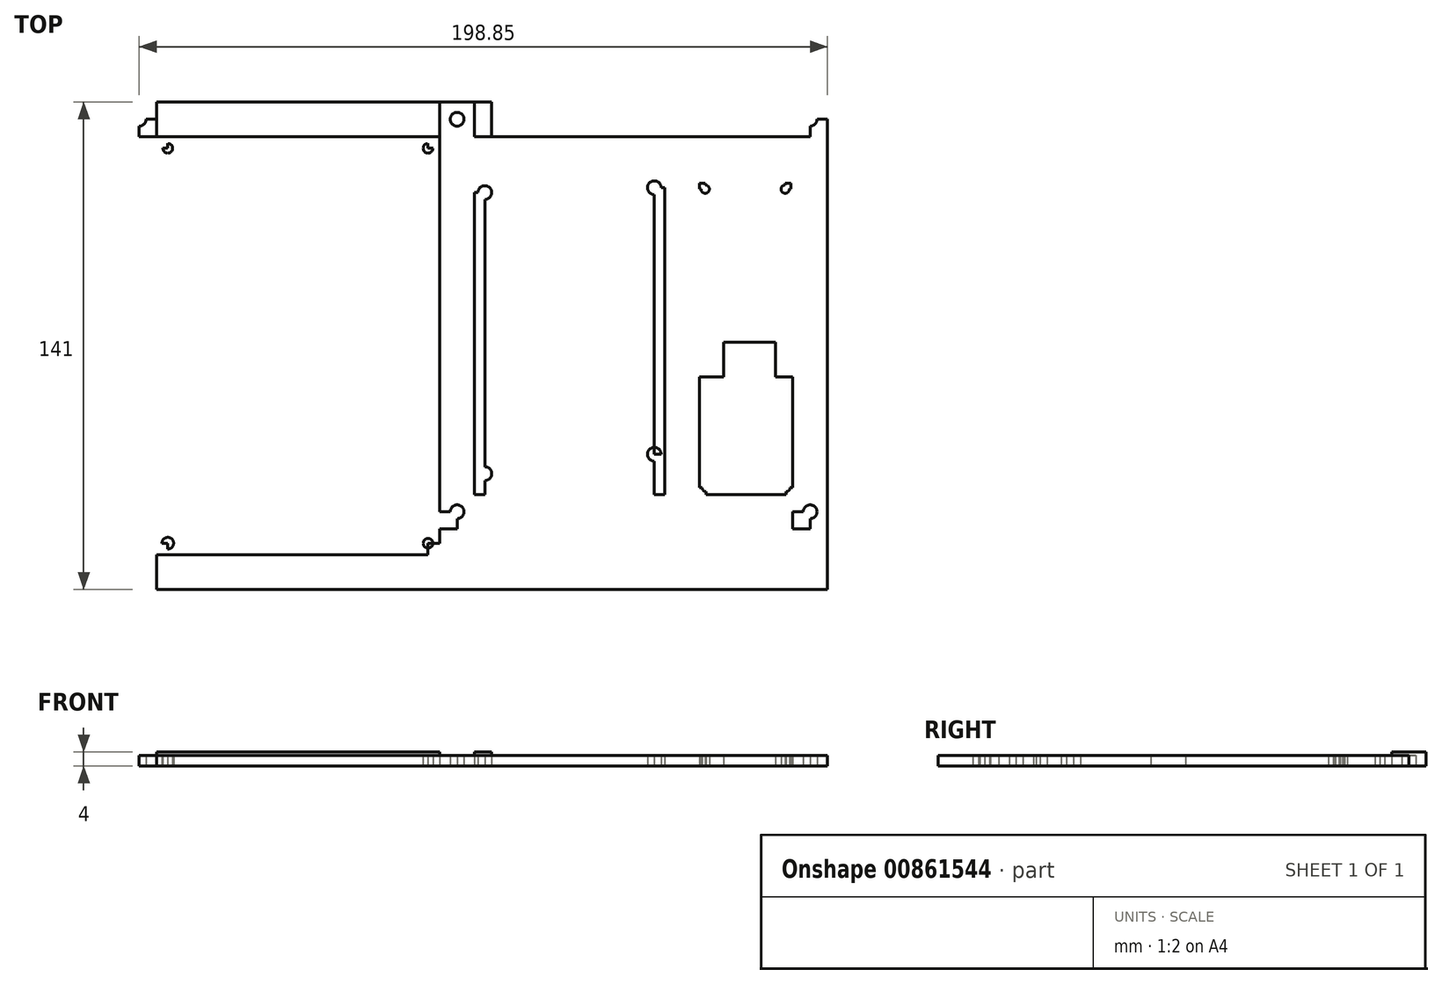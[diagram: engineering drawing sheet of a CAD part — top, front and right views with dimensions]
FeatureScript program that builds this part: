
annotation { "Feature Type Name" : "Feature", "Feature Type Description" : "" }
export const myFeature = defineFeature(function(context is Context, id is Id, definition is map)
    precondition{}
    {
        {
            var Q0;
            Q0=qCreatedBy(makeId("Top.planeOp"),FACE);
            var sketch = newSketch(context, id + "F0", { "sketchPlane" : qUnion([Q0])});
            skLineSegment(sketch, "E0.bottom", {"start": v(-139.34, -1.26) * mm, "end": v(-129.34, -1.26) * mm});
            skLineSegment(sketch, "E0.top", {"start": v(-139.34, -11.26) * mm, "end": v(-129.34, -11.26) * mm});
            skLineSegment(sketch, "E0.left", {"start": v(-139.34, -1.26) * mm, "end": v(-139.34, -11.26) * mm});
            skLineSegment(sketch, "E0.right", {"start": v(-129.34, -1.26) * mm, "end": v(-129.34, -11.26) * mm});
            skLineSegment(sketch, "E1.bottom", {"start": v(-129.34, -11.26) * mm, "end": v(-74.34, -11.26) * mm});
            skLineSegment(sketch, "E1.top", {"start": v(-129.34, -114.76) * mm, "end": v(-74.34, -114.76) * mm});
            skLineSegment(sketch, "E1.left", {"start": v(-129.34, -11.26) * mm, "end": v(-129.34, -114.76) * mm});
            skLineSegment(sketch, "E1.right", {"start": v(-74.34, -11.26) * mm, "end": v(-74.34, -114.76) * mm});
            skLineSegment(sketch, "E2", {"start": v(-74.34, -114.76) * mm, "end": v(-64.34, -114.76) * mm});
            skLineSegment(sketch, "E3.bottom", {"start": v(-64.34, -114.76) * mm, "end": v(-37.34, -114.76) * mm});
            skLineSegment(sketch, "E3.top", {"start": v(-64.34, -80.76) * mm, "end": v(-37.34, -80.76) * mm});
            skLineSegment(sketch, "E3.left", {"start": v(-64.34, -114.76) * mm, "end": v(-64.34, -80.76) * mm});
            skLineSegment(sketch, "E3.right", {"start": v(-37.34, -114.76) * mm, "end": v(-37.34, -80.76) * mm});
            skLineSegment(sketch, "E4", {"start": v(-37.34, -80.76) * mm, "end": v(-42.34, -80.76) * mm});
            skLineSegment(sketch, "E5.bottom", {"start": v(-42.34, -80.76) * mm, "end": v(-57.34, -80.76) * mm});
            skLineSegment(sketch, "E5.top", {"start": v(-42.34, -70.76) * mm, "end": v(-57.34, -70.76) * mm});
            skLineSegment(sketch, "E5.left", {"start": v(-42.34, -80.76) * mm, "end": v(-42.34, -70.76) * mm});
            skLineSegment(sketch, "E5.right", {"start": v(-57.34, -80.76) * mm, "end": v(-57.34, -70.76) * mm});
            skLineSegment(sketch, "E6", {"start": v(-64.34, -80.76) * mm, "end": v(-64.34, -60.76) * mm});
            skLineSegment(sketch, "E7.bottom", {"start": v(-64.34, -60.76) * mm, "end": v(-37.84, -60.76) * mm});
            skLineSegment(sketch, "E7.top", {"start": v(-64.34, -24.76) * mm, "end": v(-37.84, -24.76) * mm});
            skLineSegment(sketch, "E7.left", {"start": v(-64.34, -60.76) * mm, "end": v(-64.34, -24.76) * mm});
            skLineSegment(sketch, "E7.right", {"start": v(-37.84, -60.76) * mm, "end": v(-37.84, -24.76) * mm});
            skLineSegment(sketch, "E8", {"start": v(-74.34, -11.26) * mm, "end": v(-27.34, -11.26) * mm});
            skLineSegment(sketch, "E9.bottom", {"start": v(-129.34, -114.76) * mm, "end": v(-139.34, -114.76) * mm});
            skLineSegment(sketch, "E9.top", {"start": v(-129.34, -124.76) * mm, "end": v(-139.34, -124.76) * mm});
            skLineSegment(sketch, "E9.left", {"start": v(-129.34, -114.76) * mm, "end": v(-129.34, -124.76) * mm});
            skLineSegment(sketch, "E9.right", {"start": v(-139.34, -114.76) * mm, "end": v(-139.34, -124.76) * mm});
            skLineSegment(sketch, "E10.bottom", {"start": v(-37.34, -114.76) * mm, "end": v(-27.34, -114.76) * mm});
            skLineSegment(sketch, "E10.top", {"start": v(-37.34, -124.76) * mm, "end": v(-27.34, -124.76) * mm});
            skLineSegment(sketch, "E10.left", {"start": v(-37.34, -114.76) * mm, "end": v(-37.34, -124.76) * mm});
            skLineSegment(sketch, "E10.right", {"start": v(-27.34, -114.76) * mm, "end": v(-27.34, -124.76) * mm});
            skLineSegment(sketch, "E11.top", {"start": v(-139.34, -124.76) * mm, "end": v(-37.34, -124.76) * mm});
            skLineSegment(sketch, "E12", {"start": v(-129.34, -11.26) * mm, "end": v(-124.34, -11.26) * mm});
            skLineSegment(sketch, "E13", {"start": v(-124.34, -11.26) * mm, "end": v(-124.34, -1.26) * mm});
            skLineSegment(sketch, "E14", {"start": v(-74.34, -11.26) * mm, "end": v(-79.34, -11.26) * mm});
            skLineSegment(sketch, "E15", {"start": v(-79.34, -11.26) * mm, "end": v(-79.34, -1.26) * mm});
            skLineSegment(sketch, "E16.bottom", {"start": v(-129.34, -11.26) * mm, "end": v(-126.54, -11.26) * mm});
            skLineSegment(sketch, "E16.left", {"start": v(-129.34, -11.26) * mm, "end": v(-129.34, -14.06) * mm});
            skLineSegment(sketch, "E17.bottom", {"start": v(-129.34, -114.76) * mm, "end": v(-126.34, -114.76) * mm});
            skLineSegment(sketch, "E17.left", {"start": v(-129.34, -114.76) * mm, "end": v(-129.34, -111.76) * mm});
            skLineSegment(sketch, "E18.bottom", {"start": v(-74.34, -114.76) * mm, "end": v(-77.2, -114.76) * mm});
            skLineSegment(sketch, "E18.left", {"start": v(-74.34, -114.76) * mm, "end": v(-74.34, -111.9) * mm});
            skLineSegment(sketch, "E19.bottom", {"start": v(-74.34, -11.26) * mm, "end": v(-77.34, -11.26) * mm});
            skLineSegment(sketch, "E19.left", {"start": v(-74.34, -11.26) * mm, "end": v(-74.34, -14.26) * mm});
            skLineSegment(sketch, "E20.left", {"start": v(-27.34, -11.26) * mm, "end": v(-27.34, -14.66) * mm});
            skLineSegment(sketch, "E21.bottom", {"start": v(-37.84, -60.76) * mm, "end": v(-39.6, -60.76) * mm});
            skLineSegment(sketch, "E21.left", {"start": v(-37.84, -60.76) * mm, "end": v(-37.84, -59) * mm});
            skLineSegment(sketch, "E22.bottom", {"start": v(-37.84, -24.76) * mm, "end": v(-39.54, -24.76) * mm});
            skLineSegment(sketch, "E22.top", {"start": v(-37.84, -26.46) * mm, "end": v(-39.54, -26.46) * mm});
            skLineSegment(sketch, "E22.left", {"start": v(-37.84, -24.76) * mm, "end": v(-37.84, -26.46) * mm});
            skLineSegment(sketch, "E22.right", {"start": v(-39.54, -24.76) * mm, "end": v(-39.54, -26.46) * mm});
            skLineSegment(sketch, "E23.bottom", {"start": v(-64.34, -24.76) * mm, "end": v(-62.64, -24.76) * mm});
            skLineSegment(sketch, "E23.top", {"start": v(-64.34, -26.46) * mm, "end": v(-62.64, -26.46) * mm});
            skLineSegment(sketch, "E23.left", {"start": v(-64.34, -24.76) * mm, "end": v(-64.34, -26.46) * mm});
            skLineSegment(sketch, "E23.right", {"start": v(-62.64, -24.76) * mm, "end": v(-62.64, -26.46) * mm});
            skLineSegment(sketch, "E24.bottom", {"start": v(-64.34, -60.76) * mm, "end": v(-62.6, -60.76) * mm});
            skLineSegment(sketch, "E24.left", {"start": v(-64.34, -60.76) * mm, "end": v(-64.34, -59) * mm});
            skLineSegment(sketch, "E25.bottom", {"start": v(-64.34, -114.76) * mm, "end": v(-62.4, -114.76) * mm});
            skLineSegment(sketch, "E25.top", {"start": v(-64.34, -112.8) * mm, "end": v(-62.4, -112.8) * mm});
            skLineSegment(sketch, "E25.left", {"start": v(-64.34, -114.76) * mm, "end": v(-64.34, -112.8) * mm});
            skLineSegment(sketch, "E25.right", {"start": v(-62.4, -114.76) * mm, "end": v(-62.4, -112.8) * mm});
            skLineSegment(sketch, "E26.bottom", {"start": v(-37.34, -114.76) * mm, "end": v(-39.3, -114.76) * mm});
            skLineSegment(sketch, "E26.top", {"start": v(-37.34, -112.8) * mm, "end": v(-39.3, -112.8) * mm});
            skLineSegment(sketch, "E26.left", {"start": v(-37.34, -114.76) * mm, "end": v(-37.34, -112.8) * mm});
            skLineSegment(sketch, "E26.right", {"start": v(-39.3, -114.76) * mm, "end": v(-39.3, -112.8) * mm});
            skLineSegment(sketch, "E27.bottom", {"start": v(-37.34, -80.76) * mm, "end": v(-39.3, -80.76) * mm});
            skLineSegment(sketch, "E27.top", {"start": v(-37.34, -82.7) * mm, "end": v(-39.3, -82.7) * mm});
            skLineSegment(sketch, "E27.left", {"start": v(-37.34, -80.76) * mm, "end": v(-37.34, -82.7) * mm});
            skLineSegment(sketch, "E27.right", {"start": v(-39.3, -80.76) * mm, "end": v(-39.3, -82.7) * mm});
            skLineSegment(sketch, "E28.bottom", {"start": v(-64.34, -80.76) * mm, "end": v(-62.4, -80.76) * mm});
            skLineSegment(sketch, "E28.top", {"start": v(-64.34, -82.7) * mm, "end": v(-62.4, -82.7) * mm});
            skLineSegment(sketch, "E28.left", {"start": v(-64.34, -80.76) * mm, "end": v(-64.34, -82.7) * mm});
            skLineSegment(sketch, "E28.right", {"start": v(-62.4, -80.76) * mm, "end": v(-62.4, -82.7) * mm});
            skCircle(sketch, "E29", {"center": v(-39.3, -112.8) * mm, "radius": 1.15 * mm});
            skCircle(sketch, "E30", {"center": v(-62.4, -112.8) * mm, "radius": 1.15 * mm});
            skCircle(sketch, "E31", {"center": v(-62.4, -82.7) * mm, "radius": 1.15 * mm});
            skCircle(sketch, "E32", {"center": v(-39.3, -82.7) * mm, "radius": 1.15 * mm});
            skCircle(sketch, "E33", {"center": v(-62.64, -26.46) * mm, "radius": 1.2 * mm});
            skCircle(sketch, "E34", {"center": v(-39.54, -26.46) * mm, "radius": 1.2 * mm});
            skLineSegment(sketch, "E35.top", {"start": v(-37.34, -124.76) * mm, "end": v(-139.34, -124.76) * mm});
            skLineSegment(sketch, "E36.bottom", {"start": v(-139.34, -124.76) * mm, "end": v(-134.34, -124.76) * mm});
            skLineSegment(sketch, "E36.top", {"start": v(-139.34, -119.76) * mm, "end": v(-134.34, -119.76) * mm});
            skLineSegment(sketch, "E36.left", {"start": v(-139.34, -124.76) * mm, "end": v(-139.34, -119.76) * mm});
            skLineSegment(sketch, "E36.right", {"start": v(-134.34, -124.76) * mm, "end": v(-134.34, -119.76) * mm});
            skCircle(sketch, "E37", {"center": v(-134.34, -119.76) * mm, "radius": 2 * mm});
            skLineSegment(sketch, "E38.bottom", {"start": v(-37.34, -124.76) * mm, "end": v(-32.34, -124.76) * mm});
            skLineSegment(sketch, "E38.top", {"start": v(-37.34, -119.76) * mm, "end": v(-32.34, -119.76) * mm});
            skLineSegment(sketch, "E38.left", {"start": v(-37.34, -124.76) * mm, "end": v(-37.34, -119.76) * mm});
            skLineSegment(sketch, "E38.right", {"start": v(-32.34, -124.76) * mm, "end": v(-32.34, -119.76) * mm});
            skCircle(sketch, "E39", {"center": v(-32.34, -119.76) * mm, "radius": 2 * mm});
            skLineSegment(sketch, "E40.bottom", {"start": v(-139.34, -1.26) * mm, "end": v(-134.34, -1.26) * mm});
            skLineSegment(sketch, "E40.top", {"start": v(-139.34, -6.26) * mm, "end": v(-134.34, -6.26) * mm});
            skLineSegment(sketch, "E40.left", {"start": v(-139.34, -1.26) * mm, "end": v(-139.34, -6.26) * mm});
            skLineSegment(sketch, "E40.right", {"start": v(-134.34, -1.26) * mm, "end": v(-134.34, -6.26) * mm});
            skCircle(sketch, "E41", {"center": v(-134.34, -6.26) * mm, "radius": 2 * mm});
            skLineSegment(sketch, "E42.bottom", {"start": v(-129.34, -11.26) * mm, "end": v(-126.34, -11.26) * mm});
            skLineSegment(sketch, "E42.left", {"start": v(-129.34, -11.26) * mm, "end": v(-129.34, -27.96) * mm});
            skLineSegment(sketch, "E43.top", {"start": v(-129.34, -108.76) * mm, "end": v(-126.34, -108.76) * mm});
            skLineSegment(sketch, "E43.left", {"start": v(-129.34, -114.76) * mm, "end": v(-129.34, -108.76) * mm});
            skLineSegment(sketch, "E43.right", {"start": v(-126.34, -114.76) * mm, "end": v(-126.34, -108.76) * mm});
            skLineSegment(sketch, "E44.bottom", {"start": v(-74.34, -114.76) * mm, "end": v(-77.34, -114.76) * mm});
            skLineSegment(sketch, "E44.top", {"start": v(-74.34, -103.16) * mm, "end": v(-77.34, -103.16) * mm});
            skLineSegment(sketch, "E44.left", {"start": v(-74.34, -114.76) * mm, "end": v(-74.34, -103.16) * mm});
            skLineSegment(sketch, "E44.right", {"start": v(-77.34, -114.76) * mm, "end": v(-77.34, -103.16) * mm});
            skLineSegment(sketch, "E45.top", {"start": v(-74.34, -26.06) * mm, "end": v(-77.34, -26.06) * mm});
            skLineSegment(sketch, "E45.left", {"start": v(-74.34, -114.76) * mm, "end": v(-74.34, -26.06) * mm});
            skLineSegment(sketch, "E45.right", {"start": v(-77.34, -114.76) * mm, "end": v(-77.34, -26.06) * mm});
            skLineSegment(sketch, "E46.top", {"start": v(-129.34, -27.46) * mm, "end": v(-126.34, -27.46) * mm});
            skLineSegment(sketch, "E46.left", {"start": v(-129.34, -114.76) * mm, "end": v(-129.34, -27.46) * mm});
            skLineSegment(sketch, "E46.right", {"start": v(-126.34, -114.76) * mm, "end": v(-126.34, -27.46) * mm});
            skCircle(sketch, "E47", {"center": v(-126.34, -108.76) * mm, "radius": 2 * mm});
            skCircle(sketch, "E48", {"center": v(-126.34, -27.46) * mm, "radius": 2 * mm});
            skCircle(sketch, "E49", {"center": v(-77.34, -26.06) * mm, "radius": 2 * mm});
            skCircle(sketch, "E50", {"center": v(-77.34, -103.16) * mm, "radius": 2 * mm});
            skLineSegment(sketch, "E51", {"start": v(-139.34, -1.26) * mm, "end": v(-83.34, -1.26) * mm});
            skLineSegment(sketch, "E52.bottom", {"start": v(-83.34, -1.26) * mm, "end": v(-139.34, -1.26) * mm});
            skLineSegment(sketch, "E53.MirrorCS", {"start": v(-139.34, -132.26) * mm, "end": v(-139.34, -11.26) * mm});
            skLineSegment(sketch, "E54.MirrorCS", {"start": v(-221.2, -11.26) * mm, "end": v(-139.2, -11.26) * mm});
            skLineSegment(sketch, "E55.MirrorCS", {"start": v(-221.2, -132.26) * mm, "end": v(-139.2, -132.26) * mm});
            skCircle(sketch, "E56.MirrorC", {"center": v(-142.74, -128.86) * mm, "radius": 1.4 * mm});
            skCircle(sketch, "E57.MirrorC", {"center": v(-217.94, -128.86) * mm, "radius": 1.7 * mm});
            skCircle(sketch, "E58.MirrorC", {"center": v(-217.94, -14.66) * mm, "radius": 1.4 * mm});
            skCircle(sketch, "E59.MirrorC", {"center": v(-142.74, -14.66) * mm, "radius": 1.4 * mm});
            skLineSegment(sketch, "E60.MirrorCS", {"start": v(-142.74, -11.26) * mm, "end": v(-142.74, -14.66) * mm});
            skLineSegment(sketch, "E61.MirrorCS", {"start": v(-139.34, -14.66) * mm, "end": v(-142.74, -14.66) * mm});
            skLineSegment(sketch, "E62.MirrorCS", {"start": v(-217.94, -11.26) * mm, "end": v(-217.94, -14.66) * mm});
            skLineSegment(sketch, "E63.MirrorCS", {"start": v(-221.34, -14.66) * mm, "end": v(-217.94, -14.66) * mm});
            skLineSegment(sketch, "E64.MirrorCS", {"start": v(-142.74, -132.26) * mm, "end": v(-142.74, -128.86) * mm});
            skLineSegment(sketch, "E65.MirrorCS", {"start": v(-139.34, -128.86) * mm, "end": v(-142.74, -128.86) * mm});
            skLineSegment(sketch, "E66.MirrorCS", {"start": v(-221.34, -128.86) * mm, "end": v(-217.94, -128.86) * mm});
            skLineSegment(sketch, "E67.MirrorCS", {"start": v(-217.94, -132.26) * mm, "end": v(-217.94, -128.86) * mm});
            skLineSegment(sketch, "E68.MirrorCS", {"start": v(-27.34, -1.26) * mm, "end": v(-231.2, -1.26) * mm});
            skLineSegment(sketch, "E69", {"start": v(-221.2, -11.26) * mm, "end": v(-221.2, -1.26) * mm});
            skLineSegment(sketch, "E70", {"start": v(-221.2, -132.26) * mm, "end": v(-221.2, -11.26) * mm});
            skLineSegment(sketch, "E71", {"start": v(-221.2, -132.26) * mm, "end": v(-231.34, -132.26) * mm});
            skLineSegment(sketch, "E72", {"start": v(-27.34, -11.26) * mm, "end": v(-27.34, -1.26) * mm});
            skLineSegment(sketch, "E73.bottom", {"start": v(-221.2, -132.26) * mm, "end": v(-231.2, -132.26) * mm});
            skLineSegment(sketch, "E73.top", {"start": v(-221.2, -142.26) * mm, "end": v(-231.2, -142.26) * mm});
            skLineSegment(sketch, "E73.left", {"start": v(-221.2, -132.26) * mm, "end": v(-221.2, -142.26) * mm});
            skLineSegment(sketch, "E73.right", {"start": v(-231.2, -132.26) * mm, "end": v(-231.2, -142.26) * mm});
            skLineSegment(sketch, "E74.bottom", {"start": v(-221.2, -142.26) * mm, "end": v(-139.2, -142.26) * mm});
            skLineSegment(sketch, "E74.left", {"start": v(-221.2, -142.26) * mm, "end": v(-221.2, -132.26) * mm});
            skLineSegment(sketch, "E75", {"start": v(-27.34, -114.76) * mm, "end": v(-27.34, -11.26) * mm});
            skLineSegment(sketch, "E76", {"start": v(-231.2, -132.26) * mm, "end": v(-231.2, -1.26) * mm});
            skLineSegment(sketch, "E77.bottom", {"start": v(-129.34, -124.76) * mm, "end": v(-139.2, -124.76) * mm});
            skLineSegment(sketch, "E77.top", {"start": v(-129.34, -142.26) * mm, "end": v(-139.2, -142.26) * mm});
            skLineSegment(sketch, "E77.left", {"start": v(-129.34, -124.76) * mm, "end": v(-129.34, -142.26) * mm});
            skLineSegment(sketch, "E78", {"start": v(-139.2, -142.26) * mm, "end": v(-139.34, -132.26) * mm});
            skLineSegment(sketch, "E79.bottom", {"start": v(-231.2, -142.26) * mm, "end": v(-226.2, -142.26) * mm});
            skLineSegment(sketch, "E79.top", {"start": v(-231.2, -137.4) * mm, "end": v(-226.2, -137.4) * mm});
            skLineSegment(sketch, "E79.left", {"start": v(-231.2, -142.26) * mm, "end": v(-231.2, -137.4) * mm});
            skLineSegment(sketch, "E79.right", {"start": v(-226.2, -142.26) * mm, "end": v(-226.2, -137.4) * mm});
            skCircle(sketch, "E80", {"center": v(-226.2, -137.4) * mm, "radius": 2 * mm});
            skLineSegment(sketch, "E81.bottom", {"start": v(-221.2, -11.26) * mm, "end": v(-226.2, -11.26) * mm});
            skLineSegment(sketch, "E81.top", {"start": v(-221.2, -6.26) * mm, "end": v(-226.2, -6.26) * mm});
            skLineSegment(sketch, "E81.left", {"start": v(-221.2, -11.26) * mm, "end": v(-221.2, -6.26) * mm});
            skLineSegment(sketch, "E81.right", {"start": v(-226.2, -11.26) * mm, "end": v(-226.2, -6.26) * mm});
            skCircle(sketch, "E82", {"center": v(-226.2, -6.26) * mm, "radius": 2 * mm});
            skLineSegment(sketch, "E83.bottom", {"start": v(-27.34, -11.26) * mm, "end": v(-32.34, -11.26) * mm});
            skLineSegment(sketch, "E83.top", {"start": v(-27.34, -6.26) * mm, "end": v(-32.34, -6.26) * mm});
            skLineSegment(sketch, "E83.left", {"start": v(-27.34, -11.26) * mm, "end": v(-27.34, -6.26) * mm});
            skLineSegment(sketch, "E83.right", {"start": v(-32.34, -11.26) * mm, "end": v(-32.34, -6.26) * mm});
            skCircle(sketch, "E84", {"center": v(-32.34, -6.26) * mm, "radius": 2 * mm});
            skLineSegment(sketch, "E85.bottom", {"start": v(-129.34, -142.26) * mm, "end": v(-27.34, -142.26) * mm});
            skLineSegment(sketch, "E85.top", {"start": v(-129.34, -124.76) * mm, "end": v(-27.34, -124.76) * mm});
            skLineSegment(sketch, "E85.left", {"start": v(-129.34, -142.26) * mm, "end": v(-129.34, -124.76) * mm});
            skLineSegment(sketch, "E85.right", {"start": v(-27.34, -142.26) * mm, "end": v(-27.34, -124.76) * mm});
            skSolve(sketch);
        }
        {
            var Q0;
            Q0=makeQuery(id+"F0.imprint","IMPRINT",FACE,{"disambiguationData":[TD([[makeQuery(id+"F0.imprint","IMPRINT",EDGE,{"derivedFrom":sQuery(id+"F0.wireOp",EDGE,"E1.right")}),1.0]])]});
            var Q1;
            Q1=makeQuery(id+"F0.imprint","IMPRINT",FACE,{"disambiguationData":[TD([[makeQuery(id+"F0.imprint","IMPRINT",EDGE,{"derivedFrom":sQuery(id+"F0.wireOp",EDGE,"E10.bottom")}),-1.0]])]});
            var Q2;
            Q2=makeQuery(id+"F0.imprint","IMPRINT",FACE,{"disambiguationData":[TD([[makeQuery(id+"F0.imprint","IMPRINT",EDGE,{"derivedFrom":sQuery(id+"F0.wireOp",EDGE,"E1.top")}),-1.0]])]});
            var Q3;
            Q3=makeQuery(id+"F0.imprint","IMPRINT",FACE,{"disambiguationData":[TD([[makeQuery(id+"F0.imprint","IMPRINT",EDGE,{"derivedFrom":sQuery(id+"F0.wireOp",EDGE,"E9.bottom")}),1.0]])]});
            var Q4;
            Q4=makeQuery(id+"F0.imprint","IMPRINT",FACE,{"disambiguationData":[TD([[makeQuery(id+"F0.imprint","IMPRINT",EDGE,{"derivedFrom":sQuery(id+"F0.wireOp",EDGE,"97myMdQA-agTY-EE5a-eSU0-3Ky6piHqa90I.left")}),1.0]])]});
            var Q5;
            Q5=makeQuery(id+"F0.imprint","IMPRINT",FACE,{"disambiguationData":[TD([[makeQuery(id+"F0.imprint","IMPRINT",EDGE,{"derivedFrom":sQuery(id+"F0.wireOp",EDGE,"E0.bottom")}),-1.0]])]});
            var Q6;
            {var subQ0=sQuery(id+"F0.wireOp",EDGE,"E0.right");Q6=makeQuery(id+"F0.imprint","IMPRINT",FACE,{"disambiguationData":[TD([[makeQuery(id+"F0.imprint","IMPRINT",EDGE,{"derivedFrom":subQ0}),1.0]])]});}
            var Q7;
            {var subQ2=sQuery(id+"F0.wireOp",EDGE,"97myMdQA-agTY-EE5a-eSU0-3Ky6piHqa90I.right");Q7=makeQuery(id+"F0.imprint","IMPRINT",FACE,{"disambiguationData":[TD([[makeQuery(id+"F0.imprint","IMPRINT",EDGE,{"derivedFrom":subQ2}),-1.0]])]});}
            var Q8;
            {var subQ0=sQuery(id+"F0.wireOp",EDGE,"E10.top");Q8=makeQuery(id+"F0.imprint","IMPRINT",FACE,{"disambiguationData":[TD([[makeQuery(id+"F0.imprint","IMPRINT",EDGE,{"derivedFrom":subQ0}),-1.0]])]});}
            var Q9;
            {var subQ1=sQuery(id+"F0.wireOp",EDGE,"R2WY0SRa-AH7d-UwmP-SjNj-uamWJIKeu4LY.bottom");Q9=makeQuery(id+"F0.imprint","IMPRINT",FACE,{"disambiguationData":[TD([[makeQuery(id+"F0.imprint","IMPRINT",EDGE,{"derivedFrom":subQ1}),1.0]])]});}
            var Q10;
            {var subQ1=sQuery(id+"F0.wireOp",EDGE,"E36.bottom");Q10=makeQuery(id+"F0.imprint","IMPRINT",FACE,{"disambiguationData":[TD([[makeQuery(id+"F0.imprint","IMPRINT",EDGE,{"derivedFrom":subQ1}),1.0]])]});}
            var Q11;
            {var subQ1=sQuery(id+"F0.wireOp",EDGE,"E40.bottom");Q11=makeQuery(id+"F0.imprint","IMPRINT",FACE,{"disambiguationData":[TD([[makeQuery(id+"F0.imprint","IMPRINT",EDGE,{"derivedFrom":subQ1}),-1.0]])]});}
            var Q12;
            {var subQ1=sQuery(id+"F0.wireOp",EDGE,"E38.bottom");Q12=makeQuery(id+"F0.imprint","IMPRINT",FACE,{"disambiguationData":[TD([[makeQuery(id+"F0.imprint","IMPRINT",EDGE,{"derivedFrom":subQ1}),1.0]])]});}
            var Q13;
            {var subQ1=sQuery(id+"F0.wireOp",EDGE,"E77.top");Q13=makeQuery(id+"F0.imprint","IMPRINT",FACE,{"disambiguationData":[TD([[makeQuery(id+"F0.imprint","IMPRINT",EDGE,{"derivedFrom":subQ1}),-1.0]])]});}
            var Q14;
            {var subQ5=sQuery(id+"F0.wireOp",EDGE,"E74.bottom");Q14=makeQuery(id+"F0.imprint","IMPRINT",FACE,{"disambiguationData":[TD([[makeQuery(id+"F0.imprint","IMPRINT",EDGE,{"derivedFrom":subQ5}),1.0]])]});}
            var Q15;
            Q15=makeQuery(id+"F0.imprint","IMPRINT",FACE,{"disambiguationData":[TD([[makeQuery(id+"F0.imprint","IMPRINT",EDGE,{"derivedFrom":sQuery(id+"F0.wireOp",EDGE,"E73.bottom")}),1.0]])]});
            var Q16;
            {var subQ4=sQuery(id+"F0.wireOp",EDGE,"E69");Q16=makeQuery(id+"F0.imprint","IMPRINT",FACE,{"disambiguationData":[TD([[makeQuery(id+"F0.imprint","IMPRINT",EDGE,{"derivedFrom":subQ4}),1.0]])]});}
            var Q17;
            {var subQ12=sQuery(id+"F0.wireOp",EDGE,"E0.top");Q17=makeQuery(id+"F0.imprint","IMPRINT",FACE,{"disambiguationData":[TD([[makeQuery(id+"F0.imprint","IMPRINT",EDGE,{"derivedFrom":subQ12}),-1.0]])]});}
            var Q18;
            {var subQ5=sQuery(id+"F0.wireOp",EDGE,"E0.top");Q18=makeQuery(id+"F0.imprint","IMPRINT",FACE,{"disambiguationData":[TD([[makeQuery(id+"F0.imprint","IMPRINT",EDGE,{"derivedFrom":subQ5}),1.0]])]});}
            var Q19;
            Q19=makeQuery(id+"F0.imprint","IMPRINT",FACE,{"disambiguationData":[TD([[makeQuery(id+"F0.imprint","IMPRINT",EDGE,{"derivedFrom":sQuery(id+"F0.wireOp",EDGE,"E1.bottom")}),1.0]])]});
            var Q20;
            Q20=makeQuery(id+"F0.imprint","IMPRINT",FACE,{"disambiguationData":[TD([[makeQuery(id+"F0.imprint","IMPRINT",EDGE,{"derivedFrom":sQuery(id+"F0.wireOp",EDGE,"E8")}),1.0]])]});
            var Q21;
            {var subQ5=sQuery(id+"F0.wireOp",EDGE,"E40.left");Q21=makeQuery(id+"F0.imprint","IMPRINT",FACE,{"disambiguationData":[TD([[makeQuery(id+"F0.imprint","IMPRINT",EDGE,{"derivedFrom":subQ5}),1.0]])]});}
            var Q22;
            {var subQ1=sQuery(id+"F0.wireOp",EDGE,"E79.bottom");Q22=makeQuery(id+"F0.imprint","IMPRINT",FACE,{"disambiguationData":[TD([[makeQuery(id+"F0.imprint","IMPRINT",EDGE,{"derivedFrom":subQ1}),1.0]])]});}
            var Q23;
            {var subQ1=sQuery(id+"F0.wireOp",EDGE,"E83.bottom");Q23=makeQuery(id+"F0.imprint","IMPRINT",FACE,{"disambiguationData":[TD([[makeQuery(id+"F0.imprint","IMPRINT",EDGE,{"derivedFrom":subQ1}),-1.0]])]});}
            var Q24;
            {var subQ1=sQuery(id+"F0.wireOp",EDGE,"E81.bottom");Q24=makeQuery(id+"F0.imprint","IMPRINT",FACE,{"disambiguationData":[TD([[makeQuery(id+"F0.imprint","IMPRINT",EDGE,{"derivedFrom":subQ1}),-1.0]])]});}
            var Q25;
            {var subQ21=sQuery(id+"F0.wireOp",EDGE,"E53.MirrorCS");var subQ22=makeQuery(id+"F0.imprint","INTERSECT",VERTEX,{"derivedFrom":[sQuery(id+"F0.wireOp",EDGE,"E36.bottom"),subQ21]});Q25=makeQuery(id+"F0.imprint","IMPRINT",FACE,{"disambiguationData":[TD([[makeQuery(id+"F0.imprint","IMPRINT",EDGE,{"disambiguationData":[TD([[subQ22,1.0]])],"derivedFrom":subQ21}),1.0]])]});}
            var Q26;
            {var subQ3=sQuery(id+"F0.wireOp",EDGE,"E56.MirrorC");var subQ6=sQuery(id+"F0.wireOp",EDGE,"E64.MirrorCS");var subQ8=makeQuery(id+"F0.imprint","INTERSECT",VERTEX,{"derivedFrom":[subQ3,subQ6]});Q26=makeQuery(id+"F0.imprint","IMPRINT",FACE,{"disambiguationData":[TD([[makeQuery(id+"F0.imprint","IMPRINT",EDGE,{"disambiguationData":[TD([[subQ8,1.0]])],"derivedFrom":subQ3}),1.0]])]});}
            var Q27;
            {var subQ3=sQuery(id+"F0.wireOp",EDGE,"E66.MirrorCS");var subQ7=sQuery(id+"F0.wireOp",EDGE,"E57.MirrorC");var subQ9=makeQuery(id+"F0.imprint","INTERSECT",VERTEX,{"derivedFrom":[subQ7,subQ3]});Q27=makeQuery(id+"F0.imprint","IMPRINT",FACE,{"disambiguationData":[TD([[makeQuery(id+"F0.imprint","IMPRINT",EDGE,{"disambiguationData":[TD([[subQ9,1.0]])],"derivedFrom":subQ7}),1.0]])]});}
            var Q28;
            {var subQ0=sQuery(id+"F0.wireOp",EDGE,"E62.MirrorCS");var subQ3=sQuery(id+"F0.wireOp",EDGE,"E58.MirrorC");var subQ4=makeQuery(id+"F0.imprint","INTERSECT",VERTEX,{"derivedFrom":[subQ3,subQ0]});Q28=makeQuery(id+"F0.imprint","IMPRINT",FACE,{"disambiguationData":[TD([[makeQuery(id+"F0.imprint","IMPRINT",EDGE,{"disambiguationData":[TD([[subQ4,1.0]])],"derivedFrom":subQ3}),1.0]])]});}
            var Q29;
            {var subQ4=sQuery(id+"F0.wireOp",EDGE,"E0.left");Q29=makeQuery(id+"F0.imprint","IMPRINT",FACE,{"disambiguationData":[TD([[makeQuery(id+"F0.imprint","IMPRINT",EDGE,{"derivedFrom":subQ4}),-1.0]])]});}
            var Q30;
            {var subQ0=sQuery(id+"F0.wireOp",EDGE,"E60.MirrorCS");var subQ1=sQuery(id+"F0.wireOp",EDGE,"E59.MirrorC");var subQ2=makeQuery(id+"F0.imprint","INTERSECT",VERTEX,{"derivedFrom":[subQ1,subQ0]});Q30=makeQuery(id+"F0.imprint","IMPRINT",FACE,{"disambiguationData":[TD([[makeQuery(id+"F0.imprint","IMPRINT",EDGE,{"disambiguationData":[TD([[subQ2,-1.0]])],"derivedFrom":subQ1}),1.0]])]});}
            var Q31;
            Q31=makeQuery(id+"F0.imprint","IMPRINT",FACE,{"disambiguationData":[TD([[makeQuery(id+"F0.imprint","IMPRINT",EDGE,{"derivedFrom":sQuery(id+"F0.wireOp",EDGE,"E1.bottom")}),-1.0]])]});
            var Q32;
            {var subQ0=sQuery(id+"F0.wireOp",EDGE,"E46.left");var subQ3=makeQuery(id+"F0.imprint","IMPRINT",VERTEX,{"disambiguationData":[OD(1.0)],"derivedFrom":subQ0});Q32=makeQuery(id+"F0.imprint","IMPRINT",FACE,{"disambiguationData":[TD([[makeQuery(id+"F0.imprint","IMPRINT",EDGE,{"disambiguationData":[TD([[subQ3,1.0]])],"derivedFrom":subQ0}),-1.0]])]});}
            var Q33;
            {var subQ5=sQuery(id+"F0.wireOp",EDGE,"E45.left");var subQ8=sQuery(id+"F0.wireOp",EDGE,"E44.top");var subQ9=makeQuery(id+"F0.imprint","INTERSECT",VERTEX,{"derivedFrom":[subQ8,subQ5]});Q33=makeQuery(id+"F0.imprint","IMPRINT",FACE,{"disambiguationData":[TD([[makeQuery(id+"F0.imprint","IMPRINT",EDGE,{"disambiguationData":[TD([[subQ9,-1.0]])],"derivedFrom":subQ8}),-1.0]])]});}
            var Q34;
            {var subQ0=sQuery(id+"F0.wireOp",EDGE,"E45.left");var subQ3=makeQuery(id+"F0.imprint","IMPRINT",VERTEX,{"derivedFrom":subQ0});Q34=makeQuery(id+"F0.imprint","IMPRINT",FACE,{"disambiguationData":[TD([[makeQuery(id+"F0.imprint","IMPRINT",EDGE,{"disambiguationData":[TD([[subQ3,-1.0]])],"derivedFrom":subQ0}),1.0]])]});}
            var Q35;
            {var subQ1=sQuery(id+"F0.wireOp",EDGE,"E17.bottom");Q35=makeQuery(id+"F0.imprint","IMPRINT",FACE,{"disambiguationData":[TD([[makeQuery(id+"F0.imprint","IMPRINT",EDGE,{"derivedFrom":subQ1}),1.0]])]});}
            var Q36;
            {var subQ1=sQuery(id+"F0.wireOp",EDGE,"E3.bottom");Q36=makeQuery(id+"F0.imprint","IMPRINT",FACE,{"disambiguationData":[TD([[makeQuery(id+"F0.imprint","IMPRINT",EDGE,{"derivedFrom":subQ1}),1.0]])]});}
            var Q37;
            Q37=makeQuery(id+"F0.imprint","IMPRINT",FACE,{"disambiguationData":[TD([[makeQuery(id+"F0.imprint","IMPRINT",EDGE,{"derivedFrom":sQuery(id+"F0.wireOp",EDGE,"E5.bottom")}),-1.0]])]});
            var Q38;
            Q38=makeQuery(id+"F0.imprint","IMPRINT",FACE,{"disambiguationData":[TD([[makeQuery(id+"F0.imprint","IMPRINT",EDGE,{"derivedFrom":sQuery(id+"F0.wireOp",EDGE,"E7.bottom")}),1.0]])]});
            var Q39;
            {var subQ1=sQuery(id+"F0.wireOp",EDGE,"E23.bottom");Q39=makeQuery(id+"F0.imprint","IMPRINT",FACE,{"disambiguationData":[TD([[makeQuery(id+"F0.imprint","IMPRINT",EDGE,{"derivedFrom":subQ1}),-1.0]])]});}
            var Q40;
            {var subQ1=sQuery(id+"F0.wireOp",EDGE,"E22.bottom");Q40=makeQuery(id+"F0.imprint","IMPRINT",FACE,{"disambiguationData":[TD([[makeQuery(id+"F0.imprint","IMPRINT",EDGE,{"derivedFrom":subQ1}),1.0]])]});}
            var Q41;
            {var subQ1=sQuery(id+"F0.wireOp",EDGE,"E28.bottom");Q41=makeQuery(id+"F0.imprint","IMPRINT",FACE,{"disambiguationData":[TD([[makeQuery(id+"F0.imprint","IMPRINT",EDGE,{"derivedFrom":subQ1}),-1.0]])]});}
            var Q42;
            {var subQ1=sQuery(id+"F0.wireOp",EDGE,"E27.bottom");Q42=makeQuery(id+"F0.imprint","IMPRINT",FACE,{"disambiguationData":[TD([[makeQuery(id+"F0.imprint","IMPRINT",EDGE,{"derivedFrom":subQ1}),1.0]])]});}
            var Q43;
            {var subQ1=sQuery(id+"F0.wireOp",EDGE,"E25.bottom");Q43=makeQuery(id+"F0.imprint","IMPRINT",FACE,{"disambiguationData":[TD([[makeQuery(id+"F0.imprint","IMPRINT",EDGE,{"derivedFrom":subQ1}),1.0]])]});}
            var Q44;
            {var subQ1=sQuery(id+"F0.wireOp",EDGE,"E26.bottom");Q44=makeQuery(id+"F0.imprint","IMPRINT",FACE,{"disambiguationData":[TD([[makeQuery(id+"F0.imprint","IMPRINT",EDGE,{"derivedFrom":subQ1}),-1.0]])]});}
            var Q45;
            Q45=makeQuery(id+"F0.imprint","IMPRINT",FACE,{"disambiguationData":[TD([[makeQuery(id+"F0.imprint","IMPRINT",EDGE,{"derivedFrom":sQuery(id+"F0.wireOp",EDGE,"E85.bottom")}),1.0]])]});
            var Q46;
            {var subQ5=sQuery(id+"F0.wireOp",EDGE,"E38.left");Q46=makeQuery(id+"F0.imprint","IMPRINT",FACE,{"disambiguationData":[TD([[makeQuery(id+"F0.imprint","IMPRINT",EDGE,{"derivedFrom":subQ5}),-1.0]])]});}
            extrude(context, id + "F1", {"entities" : qUnion([Q0, Q1, Q2, Q3, Q4, Q5, Q6, Q7, Q8, Q9, Q10, Q11, Q12, Q13, Q14, Q15, Q16, Q17, Q18, Q19, Q20, Q21, Q22, Q23, Q24, Q25, Q26, Q27, Q28, Q29, Q30, Q31, Q32, Q33, Q34, Q35, Q36, Q37, Q38, Q39, Q40, Q41, Q42, Q43, Q44, Q45, Q46]), "depth" : 3 * mm, "offsetDistance" : 25 * mm});
        }
        {
            var Q0;
            {var subQ7=sQuery(id+"F0.wireOp",EDGE,"E0.left");Q0=makeQuery(id+"F0.imprint","IMPRINT",FACE,{"disambiguationData":[TD([[makeQuery(id+"F0.imprint","IMPRINT",EDGE,{"derivedFrom":subQ7}),-1.0]])]});}
            extrude(context, id + "F2", {"entities" : qUnion([Q0]), "operationType" : NewBodyOperationType.ADD, "depth" : 4 * mm, "offsetDistance" : 25.4 * mm});
        }
        {
            var Q0;
            Q0=makeQuery(id+"F0.imprint","IMPRINT",FACE,{"disambiguationData":[TD([[makeQuery(id+"F0.imprint","IMPRINT",EDGE,{"derivedFrom":sQuery(id+"F0.wireOp",EDGE,"E1.bottom")}),1.0]])]});
            extrude(context, id + "F3", {"entities" : qUnion([Q0]), "operationType" : NewBodyOperationType.ADD, "depth" : 4 * mm, "offsetDistance" : 25.4 * mm});
        }
    });
